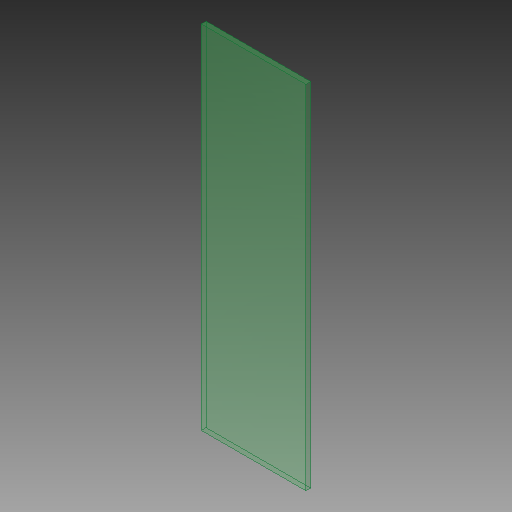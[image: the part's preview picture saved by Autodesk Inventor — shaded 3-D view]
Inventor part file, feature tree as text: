
AUTODESK INVENTOR PART (.ipt)
format: ipt  version: 2018.1 (Build 221171000, 171)  size: 93,184 bytes
history: native  units: mm
features: other x1, extrude x1, sketch x1
ambient origin geometry x8: Origin, YZ Plane, XZ Plane, XY Plane, X Axis, Y Axis, Z Axis, Center Point
bodies: Solid1 (feature_tree)
feature tree (3):
  parser-record x1  (decoder bookkeeping rows leaked as tree rows — omitted from the tree; the rows remain in map.json)
  extrude  "Extrusion1"  Depth=370.0mm
  sketch  "Sketch1"  dims[d0=110.0mm d1=370.0mm d2=5.0mm d3=0.0mm]
note: 1 file-system path scrubbed to <path> (originals preserved in map.json)
